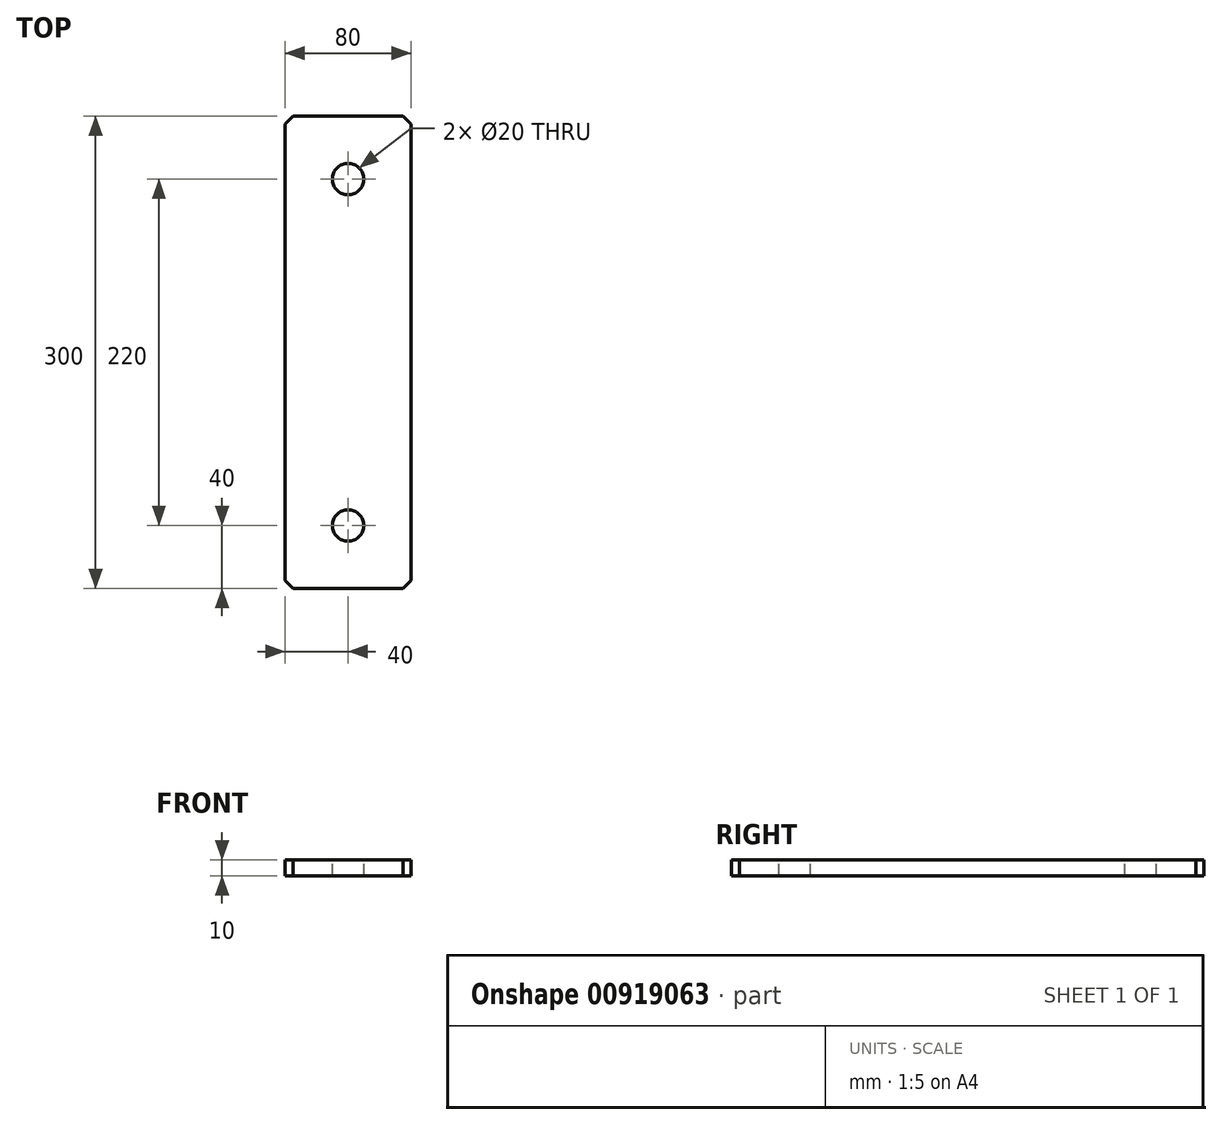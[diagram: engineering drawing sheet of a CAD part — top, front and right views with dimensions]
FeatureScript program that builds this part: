
annotation { "Feature Type Name" : "Feature", "Feature Type Description" : "" }
export const myFeature = defineFeature(function(context is Context, id is Id, definition is map)
    precondition{}
    {
        {
            var Q0;
            Q0=qCreatedBy(makeId("Top.planeOp"),FACE);
            var sketch = newSketch(context, id + "F0", { "sketchPlane" : qUnion([Q0])});
            skLineSegment(sketch, "E0.bottom", {"start": v(40, 150) * mm, "end": v(-40, 150) * mm});
            skLineSegment(sketch, "E0.top", {"start": v(40, -150) * mm, "end": v(-40, -150) * mm});
            skLineSegment(sketch, "E0.left", {"start": v(40, 150) * mm, "end": v(40, -150) * mm});
            skLineSegment(sketch, "E0.right", {"start": v(-40, 150) * mm, "end": v(-40, -150) * mm});
            skPoint(sketch, "E0.middle", {"position": v(0, 0) * mm});
            skCircle(sketch, "E1", {"center": v(0, 110) * mm, "radius": 10 * mm});
            skCircle(sketch, "E2.MirrorC", {"center": v(0, -110) * mm, "radius": 10 * mm});
            skSolve(sketch);
        }
        {
            var Q0;
            Q0=makeQuery(id+"F0.imprint","IMPRINT",FACE,{"disambiguationData":[TD([[makeQuery(id+"F0.imprint","IMPRINT",EDGE,{"derivedFrom":sQuery(id+"F0.wireOp",EDGE,"E0.bottom")}),1.0]])]});
            extrude(context, id + "F1", {"entities" : qUnion([Q0]), "oppositeDirection" : true, "depth" : 10 * mm, "offsetDistance" : 25 * mm});
        }
        {
            var Q0;
            Q0=makeQuery(id+"F1.opExtrude","SWEPT_EDGE",EDGE,{"disambiguationData":[OSD([sQuery(id+"F0.wireOp",EDGE,"E0.bottom"),sQuery(id+"F0.wireOp",EDGE,"E0.left")])]});
            var Q1;
            Q1=makeQuery(id+"F1.opExtrude","SWEPT_EDGE",EDGE,{"disambiguationData":[OSD([sQuery(id+"F0.wireOp",EDGE,"E0.top"),sQuery(id+"F0.wireOp",EDGE,"E0.left")])]});
            var Q2;
            Q2=makeQuery(id+"F1.opExtrude","SWEPT_EDGE",EDGE,{"disambiguationData":[OSD([sQuery(id+"F0.wireOp",EDGE,"E0.top"),sQuery(id+"F0.wireOp",EDGE,"E0.right")])]});
            var Q3;
            Q3=makeQuery(id+"F1.opExtrude","SWEPT_EDGE",EDGE,{"disambiguationData":[OSD([sQuery(id+"F0.wireOp",EDGE,"E0.bottom"),sQuery(id+"F0.wireOp",EDGE,"E0.right")])]});
            chamfer(context, id + "F2", {"entities" : qUnion([Q0, Q1, Q2, Q3]), "chamferType" : ChamferType.OFFSET_ANGLE, "width" : 5 * mm, "oppositeDirection" : false, "angle" : 45 * degree, "tangentPropagation" : true});
        }
    });
